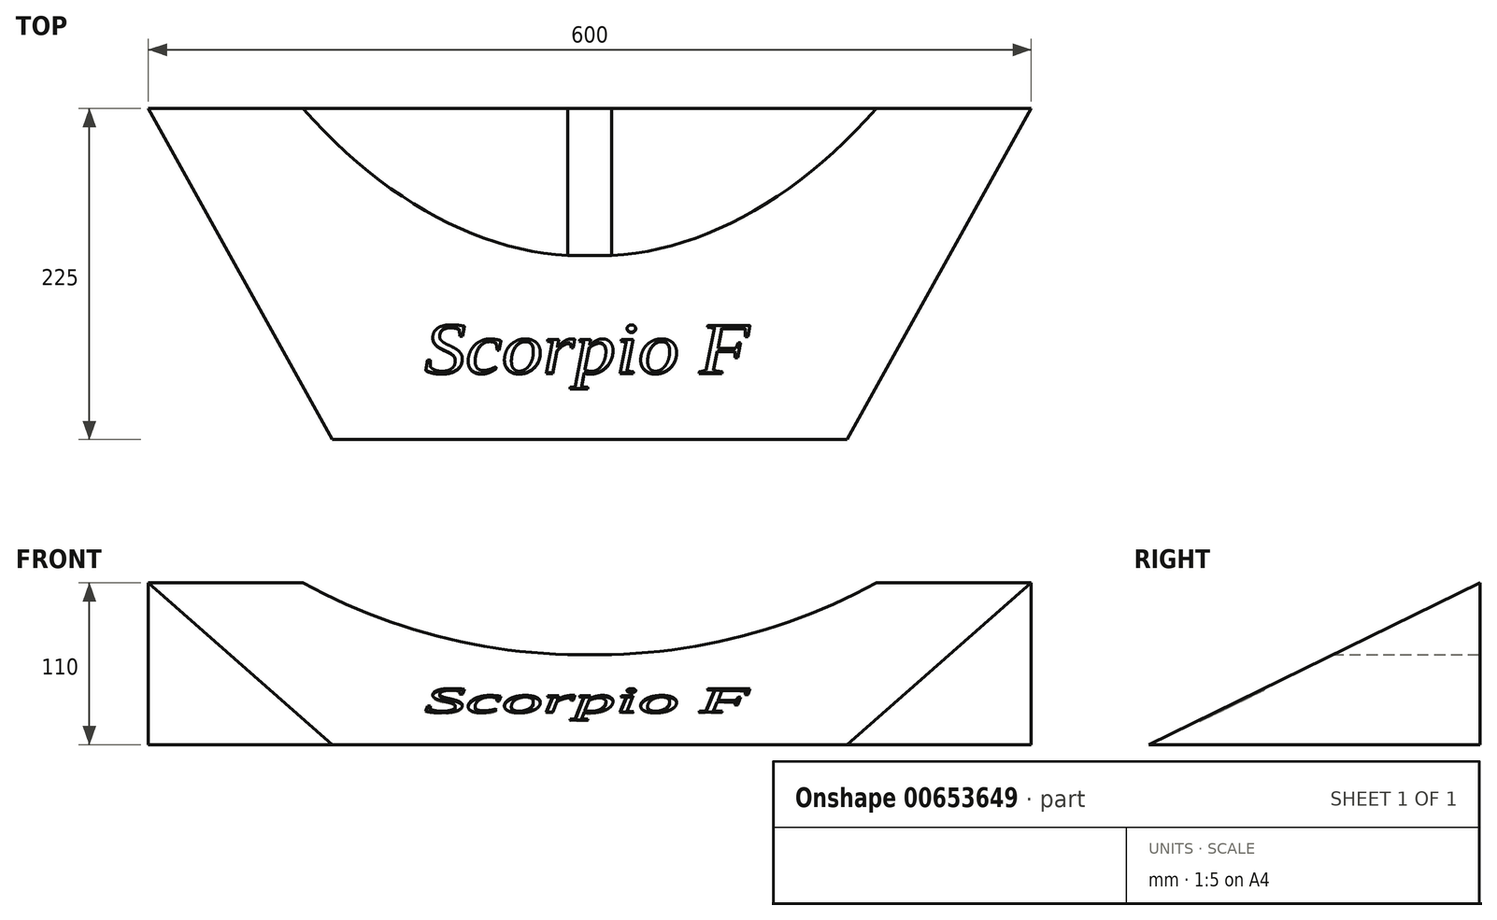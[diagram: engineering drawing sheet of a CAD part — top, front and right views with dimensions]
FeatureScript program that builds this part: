
annotation { "Feature Type Name" : "Feature", "Feature Type Description" : "" }
export const myFeature = defineFeature(function(context is Context, id is Id, definition is map)
    precondition{}
    {
        {
            var Q0;
            Q0=qCreatedBy(makeId("Top.planeOp"),FACE);
            var sketch = newSketch(context, id + "F0", { "sketchPlane" : qUnion([Q0])});
            skLineSegment(sketch, "E0", {"start": v(0, 0) * mm, "end": v(600, 0) * mm});
            skLineSegment(sketch, "E1", {"start": v(600, 0) * mm, "end": v(475, -225) * mm});
            skLineSegment(sketch, "E2", {"start": v(475, -225) * mm, "end": v(125, -225) * mm});
            skLineSegment(sketch, "E3", {"start": v(125, -225) * mm, "end": v(0, 0) * mm});
            skSolve(sketch);
        }
        {
            var Q0;
            Q0=makeQuery(id+"F0.imprint","IMPRINT",FACE,{"disambiguationData":[TD([[makeQuery(id+"F0.imprint","IMPRINT",EDGE,{"derivedFrom":sQuery(id+"F0.wireOp",EDGE,"E0")}),-1.0]])]});
            extrude(context, id + "F1", {"entities" : qUnion([Q0]), "depth" : 110 * mm, "offsetDistance" : 25 * mm});
        }
        {
            var Q0;
            Q0=qCreatedBy(makeId("Right.planeOp"),FACE);
            var sketch = newSketch(context, id + "F2", { "sketchPlane" : qUnion([Q0])});
            skLineSegment(sketch, "E4", {"start": v(-225, 0) * mm, "end": v(0, 110) * mm});
            skLineSegment(sketch, "E5", {"start": v(0, 110) * mm, "end": v(-225, 110) * mm});
            skLineSegment(sketch, "E6", {"start": v(-225, 110) * mm, "end": v(-225, 0) * mm});
            skSolve(sketch);
        }
        {
            var Q0;
            Q0 = qSketchRegion(id + "F2", true);
            extrude(context, id + "F3", {"entities" : qUnion([Q0]), "operationType" : NewBodyOperationType.REMOVE, "endBound" : BoundingType.THROUGH_ALL, "depth" : 25 * mm, "offsetDistance" : 25 * mm});
        }
        {
            var Q0;
            Q0=makeQuery(id+"F1.opExtrude","CAP_FACE",FACE,{"disambiguationData":[OSD([sQuery(id+"F0.wireOp",EDGE,"E0"),sQuery(id+"F0.wireOp",EDGE,"E1"),sQuery(id+"F0.wireOp",EDGE,"E2"),sQuery(id+"F0.wireOp",EDGE,"E3")])],"isStart":true});
            var sketch = newSketch(context, id + "F4", { "sketchPlane" : qUnion([Q0])});
            skLineSegment(sketch, "E7.bottom", {"start": v(285, 0) * mm, "end": v(315, 0) * mm});
            skLineSegment(sketch, "E7.top", {"start": v(285, 100) * mm, "end": v(315, 100) * mm});
            skLineSegment(sketch, "E7.left", {"start": v(285, 0) * mm, "end": v(285, 100) * mm});
            skLineSegment(sketch, "E7.right", {"start": v(315, 0) * mm, "end": v(315, 100) * mm});
            skSolve(sketch);
        }
        {
            var Q0;
            Q0=makeQuery(id+"F4.imprint","IMPRINT",FACE,{"disambiguationData":[TD([[makeQuery(id+"F4.imprint","IMPRINT",EDGE,{"derivedFrom":sQuery(id+"F4.wireOp",EDGE,"E7.bottom")}),1.0]])]});
            extrude(context, id + "F5", {"entities" : qUnion([Q0]), "operationType" : NewBodyOperationType.REMOVE, "endBound" : BoundingType.THROUGH_ALL, "oppositeDirection" : true, "depth" : 25 * mm, "offsetDistance" : 25 * mm});
        }
        {
            var Q0;
            {var subQ0=sQuery(id+"F0.wireOp",EDGE,"E1");var subQ1=sQuery(id+"F0.wireOp",EDGE,"E0");Q0=makeQuery(id+"F5.boolean.opBoolean","SPLIT",FACE,{"disambiguationData":[TD([makeQuery(id+"F1.opExtrude","SWEPT_FACE",FACE,{"disambiguationData":[OSD([subQ0])]})])],"derivedFrom":makeQuery(id+"F1.opExtrude","SWEPT_FACE",FACE,{"disambiguationData":[OSD([subQ1])]})});}
            var sketch = newSketch(context, id + "F6", { "sketchPlane" : qUnion([Q0])});
            skArc(sketch, "E8", {"start": v(-495, 110) * mm, "mid": v(-407.89, 74.92) * mm, "end": v(-315, 61.11) * mm});
            skArc(sketch, "E9", {"start": v(-285, 61.11) * mm, "mid": v(-192.11, 74.92) * mm, "end": v(-105, 110) * mm});
            skLineSegment(sketch, "E10", {"start": v(-285, 61.11) * mm, "end": v(-285, 110) * mm});
            skLineSegment(sketch, "E11", {"start": v(-285, 110) * mm, "end": v(-105, 110) * mm});
            skSolve(sketch);
        }
        {
            var Q0;
            Q0=makeQuery(id+"F6.imprint","IMPRINT",FACE,{"disambiguationData":[TD([[makeQuery(id+"F6.imprint","IMPRINT",EDGE,{"derivedFrom":sQuery(id+"F6.wireOp",EDGE,"E9")}),1.0]])]});
            var Q1;
            {var subQ0=sQuery(id+"F6.wireOp",EDGE,"E8");Q1=makeQuery(id+"F6.imprint","IMPRINT",FACE,{"disambiguationData":[TD([[makeQuery(id+"F6.imprint","IMPRINT",EDGE,{"derivedFrom":subQ0}),1.0]])]});}
            extrude(context, id + "F7", {"entities" : qUnion([Q0, Q1]), "operationType" : NewBodyOperationType.REMOVE, "endBound" : BoundingType.THROUGH_ALL, "oppositeDirection" : true, "depth" : 25 * mm, "offsetDistance" : 25 * mm});
        }
        {
            var Q0;
            Q0=makeQuery(id+"F5.boolean.opBoolean","COPY",FACE,{"derivedFrom":makeQuery(id+"F5.opExtrude","SWEPT_FACE",FACE,{"disambiguationData":[OSD([sQuery(id+"F4.wireOp",EDGE,"E7.top")])]})});
            var sketch = newSketch(context, id + "F8", { "sketchPlane" : qUnion([Q0])});
            skLineSegment(sketch, "E12.bottom", {"start": v(-315, 61.11) * mm, "end": v(-285, 61.11) * mm});
            skLineSegment(sketch, "E12.top", {"start": v(-315, 0) * mm, "end": v(-285, 0) * mm});
            skLineSegment(sketch, "E12.left", {"start": v(-315, 61.11) * mm, "end": v(-315, 0) * mm});
            skLineSegment(sketch, "E12.right", {"start": v(-285, 61.11) * mm, "end": v(-285, 0) * mm});
            skSolve(sketch);
        }
        {
            var Q0;
            Q0 = qSketchRegion(id + "F8", true);
            var Q1;
            {var subQ0=sQuery(id+"F0.wireOp",EDGE,"E3");var subQ1=sQuery(id+"F0.wireOp",EDGE,"E0");Q1=makeQuery(id+"F5.boolean.opBoolean","SPLIT",FACE,{"disambiguationData":[TD([makeQuery(id+"F1.opExtrude","SWEPT_FACE",FACE,{"disambiguationData":[OSD([subQ0])]})])],"derivedFrom":makeQuery(id+"F1.opExtrude","SWEPT_FACE",FACE,{"disambiguationData":[OSD([subQ1])]})});}
            extrude(context, id + "F9", {"entities" : qUnion([Q0]), "operationType" : NewBodyOperationType.ADD, "endBound" : BoundingType.UP_TO_SURFACE, "depth" : 25 * mm, "endBoundEntityFace" : qUnion([Q1]), "offsetDistance" : 25 * mm});
        }
        {
            var Q0;
            Q0=makeQuery(id+"F3.boolean.opBoolean","COPY",FACE,{"derivedFrom":makeQuery(id+"F3.opExtrude","SWEPT_FACE",FACE,{"disambiguationData":[OSD([sQuery(id+"F2.wireOp",EDGE,"E4")])]})});
            var sketch = newSketch(context, id + "F10", { "sketchPlane" : qUnion([Q0])});
            skText(sketch, "E13", { "text": "Scorpio F", "fontName": "Tinos-Italic.ttf"});
            const initialGuessF10  = {"E13": [0.1879, -0.15214, 1, 0, 0.04]};
            skSetInitialGuess(sketch, initialGuessF10);
            skSolve(sketch);
        }
        {
            var Q0;
            Q0 = qSketchRegion(id + "F10", true);
            extrude(context, id + "F11", {"entities" : qUnion([Q0]), "operationType" : NewBodyOperationType.REMOVE, "oppositeDirection" : true, "depth" : 1 * mm, "offsetDistance" : 25 * mm});
        }
    });
